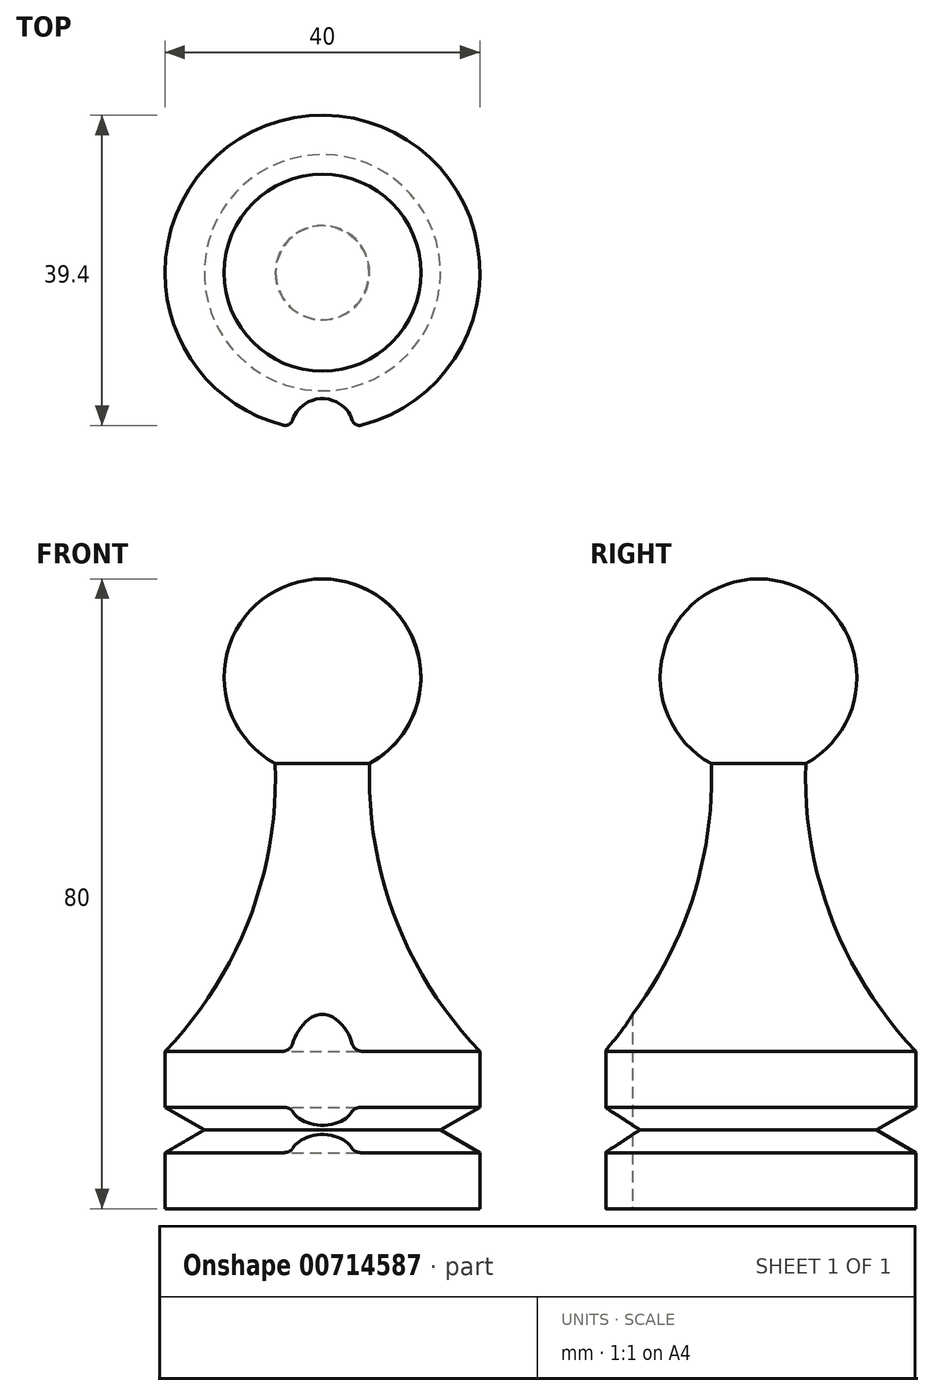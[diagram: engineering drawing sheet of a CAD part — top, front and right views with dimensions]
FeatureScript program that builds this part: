
annotation { "Feature Type Name" : "Feature", "Feature Type Description" : "" }
export const myFeature = defineFeature(function(context is Context, id is Id, definition is map)
    precondition{}
    {
        {
            var Q0;
            Q0=qCreatedBy(makeId("Front.planeOp"),FACE);
            var sketch = newSketch(context, id + "F0", { "sketchPlane" : qUnion([Q0])});
            skLineSegment(sketch, "E0", {"start": v(0, -86.74) * mm, "end": v(0, 112.4) * mm, "construction": true});
            skLineSegment(sketch, "E1", {"start": v(0, 0) * mm, "end": v(20, 0) * mm});
            skLineSegment(sketch, "E2", {"start": v(20, 0) * mm, "end": v(20, 7.11) * mm});
            skLineSegment(sketch, "E3", {"start": v(15, 10) * mm, "end": v(20, 7.11) * mm});
            skLineSegment(sketch, "E4", {"start": v(20, 12.89) * mm, "end": v(15, 10) * mm});
            skLineSegment(sketch, "E5", {"start": v(20, 12.89) * mm, "end": v(20, 20) * mm});
            skArc(sketch, "E6", {"start": v(6, 56.53) * mm, "mid": v(9.28, 36.84) * mm, "end": v(20, 20) * mm});
            skArc(sketch, "E7", {"start": v(6, 56.53) * mm, "mid": v(12.11, 70.6) * mm, "end": v(0, 80) * mm});
            skLineSegment(sketch, "E8", {"start": v(0, 80) * mm, "end": v(0, 0) * mm});
            skSolve(sketch);
        }
        {
            var Q0;
            Q0=makeQuery(id+"F0.imprint","IMPRINT",FACE,{"disambiguationData":[TD([[makeQuery(id+"F0.imprint","IMPRINT",EDGE,{"derivedFrom":sQuery(id+"F0.wireOp",EDGE,"E1")}),1.0]])]});
            var Q1;
            Q1=sQuery(id+"F0.wireOp",EDGE,"E0");
            revolve(context, id + "F1", {"surfaceOperationType" : NewSurfaceOperationType.NEW, "entities" : qUnion([Q0]), "axis" : qUnion([Q1]), "revolveType" : RevolveType.FULL});
        }
        {
            var Q0;
            Q0=makeQuery(id+"F1.opRevolve","SWEPT_FACE",FACE,{"disambiguationData":[OSD([sQuery(id+"F0.wireOp",EDGE,"E1")])]});
            var sketch = newSketch(context, id + "F2", { "sketchPlane" : qUnion([Q0])});
            skCircle(sketch, "E9", {"center": v(0, 20) * mm, "radius": 4 * mm});
            skSolve(sketch);
        }
        {
            var Q0;
            Q0 = qSketchRegion(id + "F2", true);
            extrude(context, id + "F3", {"entities" : qUnion([Q0]), "operationType" : NewBodyOperationType.REMOVE, "oppositeDirection" : true, "depth" : 35.4 * mm, "offsetDistance" : 25 * mm});
        }
        {
            var Q0;
            Q0=makeQuery(id+"F3.boolean.opBoolean","INTERSECT",EDGE,{"disambiguationData":[OD(0.0)],"derivedFrom":[makeQuery(id+"F1.opRevolve","SWEPT_FACE",FACE,{"disambiguationData":[OSD([sQuery(id+"F0.wireOp",EDGE,"E5")])]}),makeQuery(id+"F3.opExtrude","SWEPT_FACE",FACE,{"disambiguationData":[OSD([sQuery(id+"F2.wireOp",EDGE,"E9")])]})]});
            var Q1;
            Q1=makeQuery(id+"F3.boolean.opBoolean","INTERSECT",EDGE,{"disambiguationData":[OD(1.0)],"derivedFrom":[makeQuery(id+"F1.opRevolve","SWEPT_FACE",FACE,{"disambiguationData":[OSD([sQuery(id+"F0.wireOp",EDGE,"E5")])]}),makeQuery(id+"F3.opExtrude","SWEPT_FACE",FACE,{"disambiguationData":[OSD([sQuery(id+"F2.wireOp",EDGE,"E9")])]})]});
            var Q2;
            Q2=makeQuery(id+"F3.boolean.opBoolean","INTERSECT",EDGE,{"disambiguationData":[OD(0.0)],"derivedFrom":[makeQuery(id+"F1.opRevolve","SWEPT_FACE",FACE,{"disambiguationData":[OSD([sQuery(id+"F0.wireOp",EDGE,"E2")])]}),makeQuery(id+"F3.opExtrude","SWEPT_FACE",FACE,{"disambiguationData":[OSD([sQuery(id+"F2.wireOp",EDGE,"E9")])]})]});
            var Q3;
            Q3=makeQuery(id+"F3.boolean.opBoolean","INTERSECT",EDGE,{"disambiguationData":[OD(1.0)],"derivedFrom":[makeQuery(id+"F1.opRevolve","SWEPT_FACE",FACE,{"disambiguationData":[OSD([sQuery(id+"F0.wireOp",EDGE,"E2")])]}),makeQuery(id+"F3.opExtrude","SWEPT_FACE",FACE,{"disambiguationData":[OSD([sQuery(id+"F2.wireOp",EDGE,"E9")])]})]});
            fillet(context, id + "F4", {"entities" : qUnion([Q0, Q1, Q2, Q3]), "radius" : 1 * mm, "tangentPropagation" : true, "allowEdgeOverflow" : false});
        }
    });
